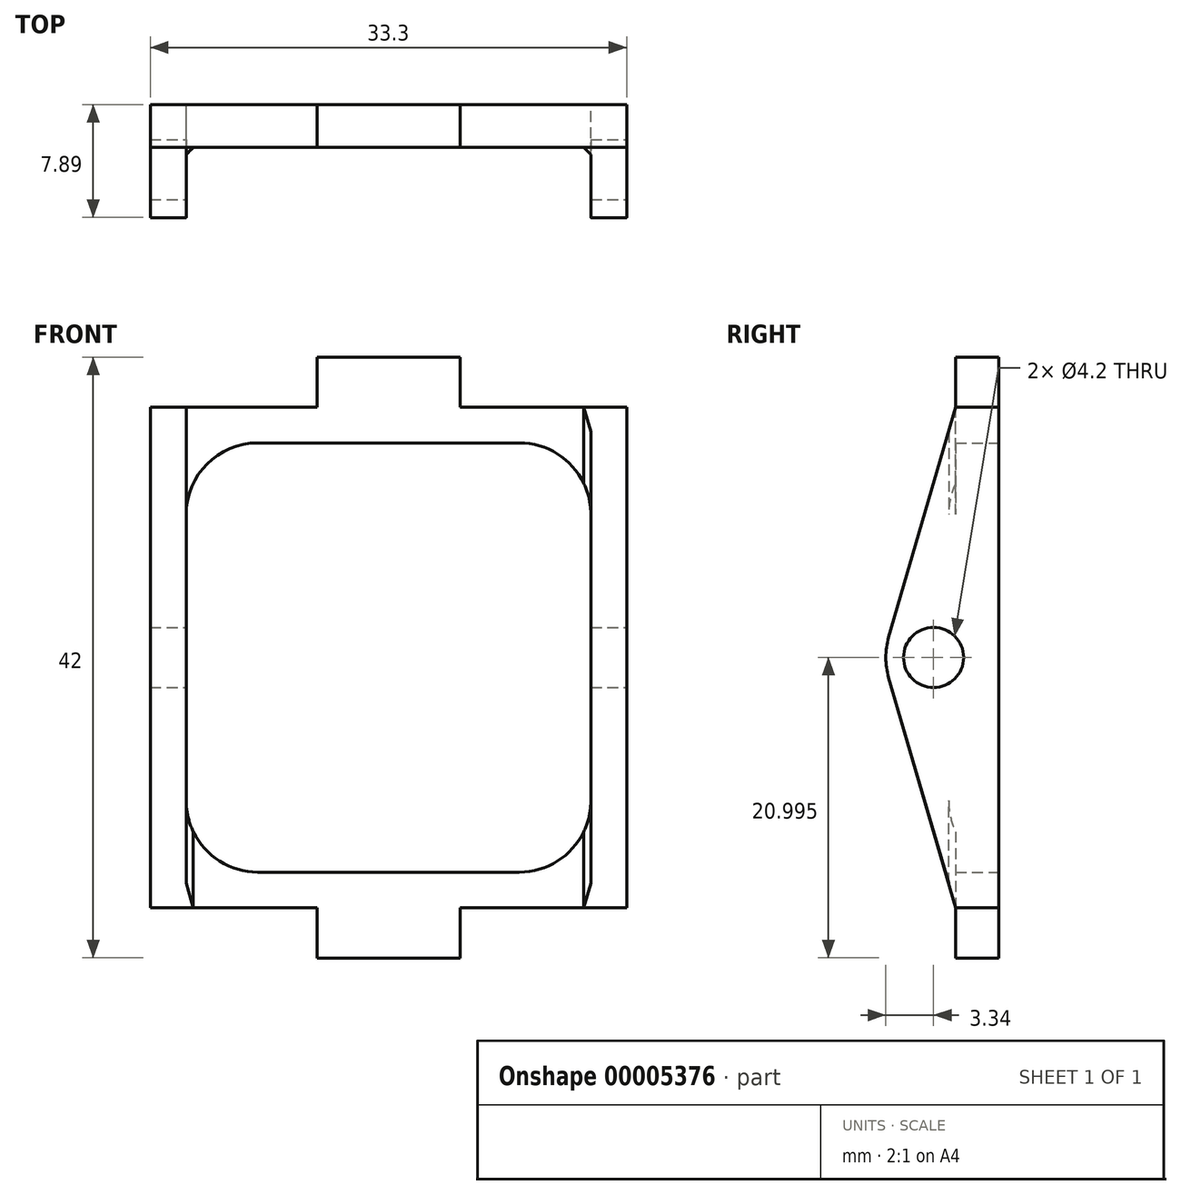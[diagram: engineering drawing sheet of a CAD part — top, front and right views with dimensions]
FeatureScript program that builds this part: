
annotation { "Feature Type Name" : "Feature", "Feature Type Description" : "" }
export const myFeature = defineFeature(function(context is Context, id is Id, definition is map)
    precondition{}
    {
        {
            var Q0;
            Q0=qCreatedBy(makeId("Front.planeOp"),FACE);
            var sketch = newSketch(context, id + "F0", { "sketchPlane" : qUnion([Q0])});
            skLineSegment(sketch, "E0", {"start": v(-29.25, 23.65) * mm, "end": v(-28.4, 23.65) * mm});
            skLineSegment(sketch, "E1", {"start": v(-29.25, 23.65) * mm, "end": v(-29.25, 27.15) * mm});
            skLineSegment(sketch, "E2", {"start": v(-29.25, 27.15) * mm, "end": v(-19.25, 27.15) * mm});
            skLineSegment(sketch, "E3", {"start": v(-19.25, 27.15) * mm, "end": v(-19.25, 23.65) * mm});
            skLineSegment(sketch, "E4", {"start": v(-19.25, 23.65) * mm, "end": v(-7.6, 23.65) * mm});
            skLineSegment(sketch, "E5", {"start": v(-7.6, 23.65) * mm, "end": v(-7.6, -11.35) * mm});
            skLineSegment(sketch, "E6", {"start": v(-40.9, -11.35) * mm, "end": v(-40.9, 23.65) * mm});
            skLineSegment(sketch, "E7", {"start": v(-40.9, 23.65) * mm, "end": v(-29.25, 23.65) * mm});
            skLineSegment(sketch, "E8.bottom", {"start": v(-38.4, 21.15) * mm, "end": v(-10.1, 21.15) * mm});
            skLineSegment(sketch, "E8.top", {"start": v(-38.4, -8.85) * mm, "end": v(-10.1, -8.85) * mm});
            skLineSegment(sketch, "E8.left", {"start": v(-38.4, 21.15) * mm, "end": v(-38.4, -8.85) * mm});
            skLineSegment(sketch, "E8.right", {"start": v(-10.1, 21.15) * mm, "end": v(-10.1, -8.85) * mm});
            skLineSegment(sketch, "E9", {"start": v(-29.25, 23.65) * mm, "end": v(-19.25, 23.65) * mm});
            skLineSegment(sketch, "E10", {"start": v(-10.1, -8.85) * mm, "end": v(-10.1, -11.35) * mm});
            skLineSegment(sketch, "E11", {"start": v(-38.4, -8.85) * mm, "end": v(-38.4, -11.35) * mm});
            skLineSegment(sketch, "E12", {"start": v(-38.4, 21.15) * mm, "end": v(-38.4, 23.65) * mm});
            skLineSegment(sketch, "E13", {"start": v(-10.1, 21.15) * mm, "end": v(-10.1, 23.65) * mm});
            skLineSegment(sketch, "E14", {"start": v(-40.9, -11.35) * mm, "end": v(-7.6, -11.35) * mm});
            skLineSegment(sketch, "E15", {"start": v(-29.25, -11.35) * mm, "end": v(-29.25, -14.85) * mm});
            skLineSegment(sketch, "E16", {"start": v(-29.25, -14.85) * mm, "end": v(-19.25, -14.85) * mm});
            skLineSegment(sketch, "E17", {"start": v(-19.25, -14.85) * mm, "end": v(-19.25, -11.35) * mm});
            skSolve(sketch);
        }
        {
            var Q0;
            {var subQ3=sQuery(id+"F0.wireOp",EDGE,"E6");Q0=makeQuery(id+"F0.imprint","IMPRINT",FACE,{"disambiguationData":[TD([[makeQuery(id+"F0.imprint","IMPRINT",EDGE,{"derivedFrom":subQ3}),-1.0]])]});}
            var Q1;
            Q1=makeQuery(id+"F0.imprint","IMPRINT",FACE,{"disambiguationData":[TD([[makeQuery(id+"F0.imprint","IMPRINT",EDGE,{"derivedFrom":sQuery(id+"F0.wireOp",EDGE,"E0")}),-1.0]])]});
            var Q2;
            {var subQ3=sQuery(id+"F0.wireOp",EDGE,"E5");Q2=makeQuery(id+"F0.imprint","IMPRINT",FACE,{"disambiguationData":[TD([[makeQuery(id+"F0.imprint","IMPRINT",EDGE,{"derivedFrom":subQ3}),-1.0]])]});}
            var Q3;
            Q3=makeQuery(id+"F0.imprint","IMPRINT",FACE,{"disambiguationData":[TD([[makeQuery(id+"F0.imprint","IMPRINT",EDGE,{"derivedFrom":sQuery(id+"F0.wireOp",EDGE,"d6d6b26c-12ba-40e5-a781-fcd901169d65")}),-1.0]])]});
            var Q4;
            Q4=makeQuery(id+"F0.imprint","IMPRINT",FACE,{"disambiguationData":[TD([[makeQuery(id+"F0.imprint","IMPRINT",EDGE,{"derivedFrom":sQuery(id+"F0.wireOp",EDGE,"E8.top")}),-1.0]])]});
            var Q5;
            {var subQ0=sQuery(id+"F0.wireOp",EDGE,"E15");Q5=makeQuery(id+"F0.imprint","IMPRINT",FACE,{"disambiguationData":[TD([[makeQuery(id+"F0.imprint","IMPRINT",EDGE,{"derivedFrom":subQ0}),1.0]])]});}
            var Q6;
            Q6=makeQuery(id+"F0.imprint","IMPRINT",FACE,{"disambiguationData":[TD([[makeQuery(id+"F0.imprint","IMPRINT",EDGE,{"derivedFrom":sQuery(id+"F0.wireOp",EDGE,"E8.bottom")}),1.0]])]});
            var Q7;
            {var subQ1=sQuery(id+"F0.wireOp",EDGE,"E1");Q7=makeQuery(id+"F0.imprint","IMPRINT",FACE,{"disambiguationData":[TD([[makeQuery(id+"F0.imprint","IMPRINT",EDGE,{"derivedFrom":subQ1}),-1.0]])]});}
            extrude(context, id + "F1", {"entities" : qUnion([Q0, Q1, Q2, Q3, Q4, Q5, Q6, Q7]), "depth" : 3 * mm});
        }
        {
            var Q0;
            Q0=makeQuery(id+"F1.opExtrude","SWEPT_FACE",FACE,{"disambiguationData":[OSD([sQuery(id+"F0.wireOp",EDGE,"E6")])]});
            var sketch = newSketch(context, id + "F2", { "sketchPlane" : qUnion([Q0])});
            skLineSegment(sketch, "E18", {"start": v(3, 23.65) * mm, "end": v(8.1, 6.15) * mm});
            skLineSegment(sketch, "E19", {"start": v(8.1, 6.15) * mm, "end": v(3, -11.35) * mm});
            skSolve(sketch);
        }
        {
            var Q0;
            Q0=makeQuery(id+"F2.imprint","IMPRINT",FACE,{"disambiguationData":[TD([[makeQuery(id+"F2.imprint","IMPRINT",EDGE,{"derivedFrom":sQuery(id+"F2.wireOp",EDGE,"f000b0cb-c19a-453c-bad9-c764841d8cd2")}),-1.0]])]});
            var Q1;
            Q1=makeQuery(id+"F2.imprint","IMPRINT",FACE,{"disambiguationData":[TD([[makeQuery(id+"F2.imprint","IMPRINT",EDGE,{"derivedFrom":sQuery(id+"F2.wireOp",EDGE,"E18")}),-1.0]])]});
            extrude(context, id + "F3", {"entities" : qUnion([Q0, Q1]), "operationType" : NewBodyOperationType.ADD, "oppositeDirection" : true, "depth" : 33.3 * mm});
        }
        {
            var Q0;
            Q0 = qSketchRegion(id + "F2", true);
            var Q1;
            Q1=makeQuery(id+"F2.imprint","IMPRINT",FACE,{"disambiguationData":[TD([[makeQuery(id+"F2.imprint","IMPRINT",EDGE,{"derivedFrom":sQuery(id+"F2.wireOp",EDGE,"E18")}),-1.0]])]});
            extrude(context, id + "F4", {"entities" : qUnion([Q0, Q1]), "operationType" : NewBodyOperationType.REMOVE, "oppositeDirection" : true, "depth" : 30.8 * mm});
        }
        {
            var Q0;
            Q0=makeQuery(id+"F2.imprint","IMPRINT",FACE,{"disambiguationData":[TD([[makeQuery(id+"F2.imprint","IMPRINT",EDGE,{"derivedFrom":sQuery(id+"F2.wireOp",EDGE,"E18")}),-1.0]])]});
            extrude(context, id + "F5", {"entities" : qUnion([Q0]), "operationType" : NewBodyOperationType.ADD, "oppositeDirection" : true, "depth" : 2.5 * mm});
        }
        {
            var Q0;
            Q0=makeQuery(id+"FQkTwnXGsS13P2U_1.boolean.opBoolean","MERGE",FACE,{"derivedFrom":[makeQuery(id+"F1.opExtrude","SWEPT_FACE",FACE,{"disambiguationData":[OSD([sQuery(id+"F0.wireOp",EDGE,"E5")])]}),makeQuery(id+"FQkTwnXGsS13P2U_1.opExtrude","CAP_FACE",FACE,{"disambiguationData":[OSD([sQuery(id+"FcwtWTbVIWFhTdg_2.wireOp",EDGE,"8f07d5ac-3ab4-4174-baa9-7eb1e79c5a4e"),sQuery(id+"FcwtWTbVIWFhTdg_2.wireOp",EDGE,"582405d9-eb13-467b-aa02-53b9b802b387"),sQuery(id+"FcwtWTbVIWFhTdg_2.wireOp",EDGE,"4234f231-25e3-41df-a1e3-b48b923457f1")])],"isStart":true})]});
            var sketch = newSketch(context, id + "F6", { "sketchPlane" : qUnion([Q0])});
            skCircle(sketch, "E20", {"center": v(-4.55, 6.15) * mm, "radius": 2.1 * mm});
            skSolve(sketch);
        }
        {
            var Q0;
            Q0=makeQuery(id+"F6.imprint","IMPRINT",FACE,{"disambiguationData":[TD([[makeQuery(id+"F6.imprint","IMPRINT",EDGE,{"derivedFrom":sQuery(id+"F6.wireOp",EDGE,"E20")}),1.0]])]});
            extrude(context, id + "F7", {"entities" : qUnion([Q0]), "operationType" : NewBodyOperationType.REMOVE, "oppositeDirection" : true, "depth" : 40 * mm});
        }
        {
            var Q0;
            {var subQ3=sQuery(id+"F0.wireOp",EDGE,"E6");var subQ5=sQuery(id+"F0.wireOp",EDGE,"E8.top");Q0=makeQuery(id+"F5.boolean.opBoolean","SPLIT",EDGE,{"disambiguationData":[TD([makeQuery(id+"F1.opExtrude","SWEPT_FACE",FACE,{"disambiguationData":[OSD([subQ5])]})])],"derivedFrom":makeQuery(id+"F5.opExtrude","CAP_EDGE",EDGE,{"disambiguationData":[OSD([subQ3])],"isStart":false})});}
            var Q1;
            {var subQ6=sQuery(id+"F0.wireOp",EDGE,"E8.top");var subQ7=sQuery(id+"F0.wireOp",EDGE,"E6");Q1=makeQuery(id+"F4.boolean.opBoolean","COPY",EDGE,{"disambiguationData":[TD([makeQuery(id+"F1.opExtrude","SWEPT_FACE",FACE,{"disambiguationData":[OSD([subQ6])]})])],"derivedFrom":makeQuery(id+"F4.opExtrude","CAP_EDGE",EDGE,{"disambiguationData":[OSD([subQ7])],"isStart":false})});}
            var Q2;
            {var subQ1=sQuery(id+"F0.wireOp",EDGE,"E4");var subQ4=sQuery(id+"F0.wireOp",EDGE,"E6");Q2=makeQuery(id+"F4.boolean.opBoolean","COPY",EDGE,{"disambiguationData":[TD([makeQuery(id+"F1.opExtrude","SWEPT_FACE",FACE,{"disambiguationData":[OSD([subQ1])]})])],"derivedFrom":makeQuery(id+"F4.opExtrude","CAP_EDGE",EDGE,{"disambiguationData":[OSD([subQ4])],"isStart":false})});}
            var Q3;
            {var subQ2=sQuery(id+"F0.wireOp",EDGE,"E6");var subQ3=sQuery(id+"F0.wireOp",EDGE,"E7");Q3=makeQuery(id+"F5.boolean.opBoolean","SPLIT",EDGE,{"disambiguationData":[TD([makeQuery(id+"F1.opExtrude","SWEPT_FACE",FACE,{"disambiguationData":[OSD([subQ3])]})])],"derivedFrom":makeQuery(id+"F5.opExtrude","CAP_EDGE",EDGE,{"disambiguationData":[OSD([subQ2])],"isStart":false})});}
            chamfer(context, id + "F8", {"entities" : qUnion([Q0, Q1, Q2, Q3]), "width" : .5 * mm, "tangentPropagation" : true});
        }
        {
            var Q0;
            Q0=makeQuery(id+"F1.opExtrude","SWEPT_EDGE",EDGE,{"disambiguationData":[OSD([sQuery(id+"F0.wireOp",EDGE,"E8.top"),sQuery(id+"F0.wireOp",EDGE,"E8.left"),sQuery(id+"F0.wireOp",EDGE,"E11")])]});
            var Q1;
            Q1=makeQuery(id+"F1.opExtrude","SWEPT_EDGE",EDGE,{"disambiguationData":[OSD([sQuery(id+"F0.wireOp",EDGE,"E8.bottom"),sQuery(id+"F0.wireOp",EDGE,"E8.left"),sQuery(id+"F0.wireOp",EDGE,"E12")])]});
            var Q2;
            Q2=makeQuery(id+"F1.opExtrude","SWEPT_EDGE",EDGE,{"disambiguationData":[OSD([sQuery(id+"F0.wireOp",EDGE,"E8.bottom"),sQuery(id+"F0.wireOp",EDGE,"E8.right"),sQuery(id+"F0.wireOp",EDGE,"E13")])]});
            var Q3;
            Q3=makeQuery(id+"F1.opExtrude","SWEPT_EDGE",EDGE,{"disambiguationData":[OSD([sQuery(id+"F0.wireOp",EDGE,"E8.top"),sQuery(id+"F0.wireOp",EDGE,"E8.right"),sQuery(id+"F0.wireOp",EDGE,"E10")])]});
            var Q4;
            Q4=makeQuery(id+"F5.opExtrude","SWEPT_EDGE",EDGE,{"disambiguationData":[OSD([sQuery(id+"F2.wireOp",EDGE,"E18"),sQuery(id+"F2.wireOp",EDGE,"E19")])]});
            var Q5;
            Q5=makeQuery(id+"F3.opExtrude","SWEPT_EDGE",EDGE,{"disambiguationData":[OSD([sQuery(id+"F2.wireOp",EDGE,"E18"),sQuery(id+"F2.wireOp",EDGE,"E19")])]});
            fillet(context, id + "F9", {"entities" : qUnion([Q0, Q1, Q2, Q3, Q4, Q5]), "radius" : 5 * mm, "tangentPropagation" : true, "allowEdgeOverflow" : false});
        }
    });
